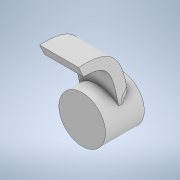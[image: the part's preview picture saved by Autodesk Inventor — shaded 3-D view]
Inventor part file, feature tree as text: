
AUTODESK INVENTOR PART (.ipt)
format: ipt  version: 2021 (Build 250183000, 183)  size: 160,768 bytes
history: native  units: mm
features: sketch x3, extrude x1, sweep x1, fillet x1
ambient origin geometry x8: Origin, YZ Plane, XZ Plane, XY Plane, X Axis, Y Axis, Z Axis, Center Point
bodies: Solid1 (feature_tree)
feature tree (6):
  extrude  "Extrusion1"  Depth=10.0mm TaperAngle=0.0deg
  sweep  "Sweep1"
  fillet  "Fillet1"  Radius=3.0mm
  sketch  "Sketch1"  dims[d0=12.0mm d1=10.0mm d2=0.0mm]
  sketch  "Sketch2"  dims[d3=15.0mm d4=10.0mm d5=3.0mm]
  sketch  "Sketch3"  dims[d6=0.0mm d7=0.0mm d8=2.0mm]
